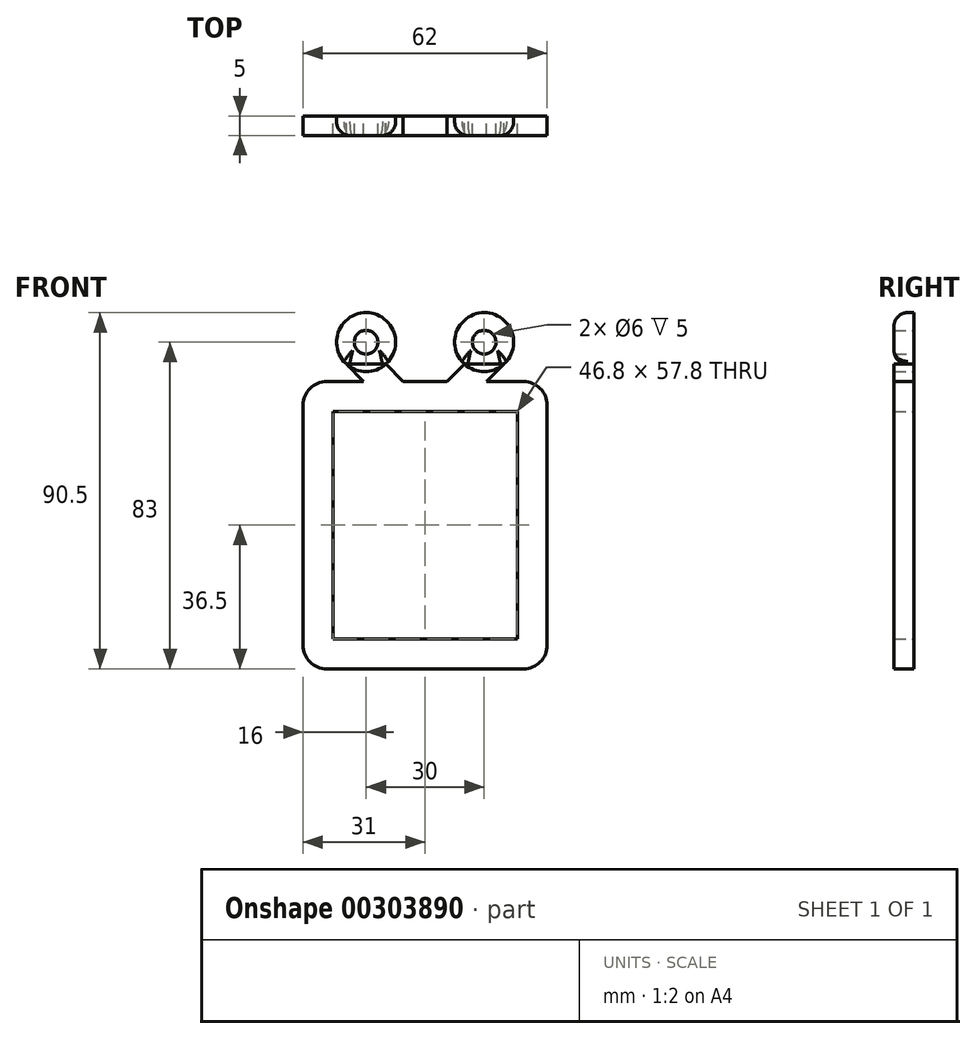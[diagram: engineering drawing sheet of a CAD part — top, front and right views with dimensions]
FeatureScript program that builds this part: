
annotation { "Feature Type Name" : "Feature", "Feature Type Description" : "" }
export const myFeature = defineFeature(function(context is Context, id is Id, definition is map)
    precondition{}
    {
        {
            var Q0;
            Q0=qCreatedBy(makeId("Front.planeOp"),FACE);
            var sketch = newSketch(context, id + "F5", { "sketchPlane" : qUnion([Q0])});
            skLineSegment(sketch, "E0.bottom", {"start": v(31, -8) * mm, "end": v(-31, -8) * mm});
            skLineSegment(sketch, "E0.top", {"start": v(31, 65) * mm, "end": v(-31, 65) * mm});
            skLineSegment(sketch, "E0.left", {"start": v(31, -8) * mm, "end": v(31, 65) * mm});
            skLineSegment(sketch, "E0.right", {"start": v(-31, -8) * mm, "end": v(-31, 65) * mm});
            skCircle(sketch, "E1", {"center": v(-15, 75) * mm, "radius": 3 * mm});
            skCircle(sketch, "E2", {"center": v(15, 75) * mm, "radius": 3 * mm});
            skLineSegment(sketch, "E3", {"start": v(0, 65) * mm, "end": v(-15, 65) * mm});
            skLineSegment(sketch, "E4", {"start": v(0, 65) * mm, "end": v(15, 65) * mm});
            skCircle(sketch, "E5", {"center": v(15, 75) * mm, "radius": 7.5 * mm});
            skCircle(sketch, "E6", {"center": v(-15, 75) * mm, "radius": 7.5 * mm});
            skLineSegment(sketch, "E7.bottom", {"start": v(-20, 69.4) * mm, "end": v(-10, 69.4) * mm});
            skLineSegment(sketch, "E7.top", {"start": v(-20, 65) * mm, "end": v(-10, 65) * mm});
            skLineSegment(sketch, "E7.left", {"start": v(-20, 69.4) * mm, "end": v(-20, 65) * mm, "construction": true});
            skLineSegment(sketch, "E7.right", {"start": v(-10, 69.4) * mm, "end": v(-10, 65) * mm, "construction": true});
            skLineSegment(sketch, "E8.bottom", {"start": v(10, 69.4) * mm, "end": v(20, 69.4) * mm});
            skLineSegment(sketch, "E8.top", {"start": v(10, 65) * mm, "end": v(20, 65) * mm});
            skLineSegment(sketch, "E8.left", {"start": v(10, 69.4) * mm, "end": v(10, 65) * mm, "construction": true});
            skLineSegment(sketch, "E8.right", {"start": v(20, 69.4) * mm, "end": v(20, 65) * mm, "construction": true});
            skLineSegment(sketch, "E9.0", {"start": v(-23, 0) * mm, "end": v(-23, 57) * mm});
            skLineSegment(sketch, "E9.1", {"start": v(23, 0) * mm, "end": v(-23, 0) * mm});
            skLineSegment(sketch, "E9.2", {"start": v(23, 0) * mm, "end": v(23, 57) * mm});
            skLineSegment(sketch, "E9.3", {"start": v(23, 57) * mm, "end": v(-23, 57) * mm});
            skLineSegment(sketch, "E10", {"start": v(-20, 69.4) * mm, "end": v(-15.6, 65) * mm});
            skLineSegment(sketch, "E11", {"start": v(20, 69.4) * mm, "end": v(15.6, 65) * mm});
            skLineSegment(sketch, "E12", {"start": v(-15, 75) * mm, "end": v(-15, 65) * mm, "construction": true});
            skLineSegment(sketch, "E13", {"start": v(15, 75) * mm, "end": v(15, 65) * mm, "construction": true});
            skLineSegment(sketch, "E14", {"start": v(-10, 69.4) * mm, "end": v(-5.6, 65) * mm});
            skLineSegment(sketch, "E15", {"start": v(10, 69.4) * mm, "end": v(5.6, 65) * mm});
            skSolve(sketch);
        }
        {
            var Q0;
            Q0=makeQuery(id+"F5.imprint","IMPRINT",FACE,{"disambiguationData":[TD([[makeQuery(id+"F5.imprint","IMPRINT",EDGE,{"derivedFrom":sQuery(id+"F5.wireOp",EDGE,"E2")}),-1.0]])]});
            var Q1;
            Q1=makeQuery(id+"F5.imprint","IMPRINT",FACE,{"disambiguationData":[TD([[makeQuery(id+"F5.imprint","IMPRINT",EDGE,{"derivedFrom":sQuery(id+"F5.wireOp",EDGE,"E1")}),-1.0]])]});
            var Q2;
            {var subQ0=sQuery(id+"F5.wireOp",EDGE,"E8.left");Q2=makeQuery(id+"F5.imprint","IMPRINT",FACE,{"disambiguationData":[TD([[makeQuery(id+"F5.imprint","IMPRINT",EDGE,{"derivedFrom":subQ0}),1.0]])]});}
            var Q3;
            Q3=makeQuery(id+"F5.imprint","IMPRINT",FACE,{"disambiguationData":[TD([[makeQuery(id+"F5.imprint","IMPRINT",EDGE,{"derivedFrom":sQuery(id+"F5.wireOp",EDGE,"E0.bottom")}),-1.0]])]});
            var Q4;
            {var subQ0=sQuery(id+"F5.wireOp",EDGE,"E7.bottom");Q4=makeQuery(id+"F5.imprint","IMPRINT",FACE,{"disambiguationData":[TD([[makeQuery(id+"F5.imprint","IMPRINT",EDGE,{"derivedFrom":subQ0}),-1.0]])]});}
            var Q5;
            {var subQ0=sQuery(id+"F5.wireOp",EDGE,"E8.bottom");Q5=makeQuery(id+"F5.imprint","IMPRINT",FACE,{"disambiguationData":[TD([[makeQuery(id+"F5.imprint","IMPRINT",EDGE,{"derivedFrom":subQ0}),-1.0]])]});}
            var Q6;
            {var subQ3=sQuery(id+"F5.wireOp",EDGE,"E7.left");Q6=makeQuery(id+"F5.imprint","IMPRINT",FACE,{"disambiguationData":[TD([[makeQuery(id+"F5.imprint","IMPRINT",EDGE,{"derivedFrom":subQ3}),1.0]])]});}
            var Q7;
            {var subQ6=sQuery(id+"F5.wireOp",EDGE,"9cc08256-3233-4f75-9d2b-67273aa2315f");Q7=makeQuery(id+"F5.imprint","IMPRINT",FACE,{"disambiguationData":[TD([[makeQuery(id+"F5.imprint","IMPRINT",EDGE,{"derivedFrom":subQ6}),-1.0]])]});}
            var Q8;
            {var subQ8=sQuery(id+"F5.wireOp",EDGE,"1ab97ab7-0e0f-4c3b-988b-f68c05d128eb");Q8=makeQuery(id+"F5.imprint","IMPRINT",FACE,{"disambiguationData":[TD([[makeQuery(id+"F5.imprint","IMPRINT",EDGE,{"derivedFrom":subQ8}),-1.0]])]});}
            extrude(context, id + "F0", {"entities" : qUnion([Q0, Q1, Q2, Q3, Q4, Q5, Q6, Q7, Q8]), "depth" : 5 * mm});
        }
        {
            var Q0;
            Q0=makeQuery(id+"F0.opExtrude","SWEPT_EDGE",EDGE,{"disambiguationData":[OSD([sQuery(id+"F5.wireOp",EDGE,"E4"),sQuery(id+"F5.wireOp",EDGE,"1ab97ab7-0e0f-4c3b-988b-f68c05d128eb")])]});
            var Q1;
            Q1=makeQuery(id+"F0.opExtrude","SWEPT_EDGE",EDGE,{"disambiguationData":[OSD([sQuery(id+"F5.wireOp",EDGE,"E5"),sQuery(id+"F5.wireOp",EDGE,"E8.bottom"),sQuery(id+"F5.wireOp",EDGE,"1ab97ab7-0e0f-4c3b-988b-f68c05d128eb")])]});
            var Q2;
            Q2=makeQuery(id+"F0.opExtrude","SWEPT_EDGE",EDGE,{"disambiguationData":[OSD([sQuery(id+"F5.wireOp",EDGE,"E5"),sQuery(id+"F5.wireOp",EDGE,"E8.bottom"),sQuery(id+"F5.wireOp",EDGE,"E11")])]});
            var Q3;
            Q3=makeQuery(id+"F0.opExtrude","SWEPT_EDGE",EDGE,{"disambiguationData":[OSD([sQuery(id+"F5.wireOp",EDGE,"E6"),sQuery(id+"F5.wireOp",EDGE,"E7.bottom"),sQuery(id+"F5.wireOp",EDGE,"E10")])]});
            var Q4;
            Q4=makeQuery(id+"F0.opExtrude","SWEPT_EDGE",EDGE,{"disambiguationData":[OSD([sQuery(id+"F5.wireOp",EDGE,"E6"),sQuery(id+"F5.wireOp",EDGE,"E7.bottom"),sQuery(id+"F5.wireOp",EDGE,"9cc08256-3233-4f75-9d2b-67273aa2315f")])]});
            var Q5;
            Q5=makeQuery(id+"F0.opExtrude","SWEPT_EDGE",EDGE,{"disambiguationData":[OSD([sQuery(id+"F5.wireOp",EDGE,"E5"),sQuery(id+"F5.wireOp",EDGE,"E8.bottom"),sQuery(id+"F5.wireOp",EDGE,"1ab97ab7-0e0f-4c3b-988b-f68c05d128eb")])]});
            var Q6;
            Q6=makeQuery(id+"F0.opExtrude","SWEPT_EDGE",EDGE,{"disambiguationData":[OSD([sQuery(id+"F5.wireOp",EDGE,"E5"),sQuery(id+"F5.wireOp",EDGE,"E8.bottom"),sQuery(id+"F5.wireOp",EDGE,"E11")])]});
            var Q7;
            Q7=makeQuery(id+"F0.opExtrude","SWEPT_EDGE",EDGE,{"disambiguationData":[OSD([sQuery(id+"F5.wireOp",EDGE,"E6"),sQuery(id+"F5.wireOp",EDGE,"E7.bottom"),sQuery(id+"F5.wireOp",EDGE,"E10")])]});
            var Q8;
            Q8=makeQuery(id+"F0.opExtrude","SWEPT_EDGE",EDGE,{"disambiguationData":[OSD([sQuery(id+"F5.wireOp",EDGE,"E6"),sQuery(id+"F5.wireOp",EDGE,"E7.bottom"),sQuery(id+"F5.wireOp",EDGE,"9cc08256-3233-4f75-9d2b-67273aa2315f")])]});
            var Q9;
            Q9=makeQuery(id+"F0.opExtrude","SWEPT_EDGE",EDGE,{"disambiguationData":[OSD([sQuery(id+"F5.wireOp",EDGE,"E7.top"),sQuery(id+"F5.wireOp",EDGE,"E10")])]});
            var Q10;
            Q10=makeQuery(id+"F0.opExtrude","SWEPT_EDGE",EDGE,{"disambiguationData":[OSD([sQuery(id+"F5.wireOp",EDGE,"E8.top"),sQuery(id+"F5.wireOp",EDGE,"E11")])]});
            var Q11;
            Q11=makeQuery(id+"F0.opExtrude","SWEPT_EDGE",EDGE,{"disambiguationData":[OSD([sQuery(id+"F5.wireOp",EDGE,"E3"),sQuery(id+"F5.wireOp",EDGE,"9cc08256-3233-4f75-9d2b-67273aa2315f")])]});
            fillet(context, id + "F1", {"entities" : qUnion([Q0, Q1, Q2, Q3, Q4, Q5, Q6, Q7, Q8, Q9, Q10, Q11]), "radius" : 2 * mm, "tangentPropagation" : true, "allowEdgeOverflow" : false});
        }
        {
            var Q0;
            Q0=makeQuery(id+"F0.opExtrude","CAP_EDGE",EDGE,{"disambiguationData":[OSD([sQuery(id+"F5.wireOp",EDGE,"E5")])],"isStart":false});
            var Q1;
            Q1=makeQuery(id+"F0.opExtrude","CAP_EDGE",EDGE,{"disambiguationData":[OSD([sQuery(id+"F5.wireOp",EDGE,"E6")])],"isStart":false});
            var Q2;
            Q2=makeQuery(id+"F0.opExtrude","CAP_EDGE",EDGE,{"disambiguationData":[OSD([sQuery(id+"F5.wireOp",EDGE,"E8.right")])],"isStart":false});
            var Q3;
            Q3=makeQuery(id+"F0.opExtrude","CAP_EDGE",EDGE,{"disambiguationData":[OSD([sQuery(id+"F5.wireOp",EDGE,"E0.left")])],"isStart":false});
            var Q4;
            Q4=makeQuery(id+"F0.opExtrude","CAP_EDGE",EDGE,{"disambiguationData":[OSD([sQuery(id+"F5.wireOp",EDGE,"E3"),sQuery(id+"F5.wireOp",EDGE,"E4")])],"isStart":false});
            var Q5;
            {var subQ0=sQuery(id+"F5.wireOp",EDGE,"E0.top");Q5=makeQuery(id+"F0.opExtrude","CAP_EDGE",EDGE,{"disambiguationData":[OSD([subQ0]),TDD([makeQuery(id+"F5.imprint","IMPRINT",EDGE,{"disambiguationData":[TD([[makeQuery(id+"F5.imprint","INTERSECT",VERTEX,{"derivedFrom":[subQ0,sQuery(id+"F5.wireOp",EDGE,"E0.right")]}),1.0]])],"derivedFrom":subQ0})])],"isStart":false});}
            var Q6;
            Q6=makeQuery(id+"F0.opExtrude","CAP_EDGE",EDGE,{"disambiguationData":[OSD([sQuery(id+"F5.wireOp",EDGE,"E7.left")])],"isStart":false});
            var Q7;
            Q7=makeQuery(id+"F0.opExtrude","CAP_EDGE",EDGE,{"disambiguationData":[OSD([sQuery(id+"F5.wireOp",EDGE,"E7.right")])],"isStart":false});
            var Q8;
            Q8=makeQuery(id+"F0.opExtrude","CAP_EDGE",EDGE,{"disambiguationData":[OSD([sQuery(id+"F5.wireOp",EDGE,"E8.left")])],"isStart":false});
            var Q9;
            Q9=makeQuery(id+"F0.opExtrude","CAP_EDGE",EDGE,{"disambiguationData":[OSD([sQuery(id+"F5.wireOp",EDGE,"E0.right")])],"isStart":false});
            var Q10;
            Q10=makeQuery(id+"F0.opExtrude","CAP_EDGE",EDGE,{"disambiguationData":[OSD([sQuery(id+"F5.wireOp",EDGE,"E0.bottom")])],"isStart":false});
            var Q11;
            {var subQ0=sQuery(id+"F5.wireOp",EDGE,"E0.top");Q11=makeQuery(id+"F0.opExtrude","CAP_EDGE",EDGE,{"disambiguationData":[OSD([subQ0]),TDD([makeQuery(id+"F5.imprint","IMPRINT",EDGE,{"disambiguationData":[TD([[makeQuery(id+"F5.imprint","INTERSECT",VERTEX,{"derivedFrom":[subQ0,sQuery(id+"F5.wireOp",EDGE,"E0.left")]}),-1.0]])],"derivedFrom":subQ0})])],"isStart":false});}
            fillet(context, id + "F2", {"entities" : qUnion([Q0, Q1, Q2, Q3, Q4, Q5, Q6, Q7, Q8, Q9, Q10, Q11]), "radius" : 3.5 * mm, "tangentPropagation" : true, "allowEdgeOverflow" : false});
        }
        {
            var Q0;
            Q0=makeQuery(id+"F0.opExtrude","SWEPT_EDGE",EDGE,{"disambiguationData":[OSD([sQuery(id+"F5.wireOp",EDGE,"E0.bottom"),sQuery(id+"F5.wireOp",EDGE,"E0.right")])]});
            var Q1;
            Q1=makeQuery(id+"F0.opExtrude","SWEPT_EDGE",EDGE,{"disambiguationData":[OSD([sQuery(id+"F5.wireOp",EDGE,"E0.top"),sQuery(id+"F5.wireOp",EDGE,"E0.right")])]});
            var Q2;
            Q2=makeQuery(id+"F0.opExtrude","SWEPT_EDGE",EDGE,{"disambiguationData":[OSD([sQuery(id+"F5.wireOp",EDGE,"E0.top"),sQuery(id+"F5.wireOp",EDGE,"E0.left")])]});
            var Q3;
            Q3=makeQuery(id+"F0.opExtrude","SWEPT_EDGE",EDGE,{"disambiguationData":[OSD([sQuery(id+"F5.wireOp",EDGE,"E0.bottom"),sQuery(id+"F5.wireOp",EDGE,"E0.left")])]});
            fillet(context, id + "F3", {"entities" : qUnion([Q0, Q1, Q2, Q3]), "radius" : 6 * mm, "tangentPropagation" : true, "allowEdgeOverflow" : false});
        }
        {
            var Q0;
            Q0=makeQuery(id+"F0.opExtrude","SWEPT_EDGE",EDGE,{"disambiguationData":[OSD([sQuery(id+"F5.wireOp",EDGE,"E9.0"),sQuery(id+"F5.wireOp",EDGE,"E9.3")])]});
            var Q1;
            Q1=makeQuery(id+"F0.opExtrude","SWEPT_EDGE",EDGE,{"disambiguationData":[OSD([sQuery(id+"F5.wireOp",EDGE,"E9.2"),sQuery(id+"F5.wireOp",EDGE,"E9.3")])]});
            var Q2;
            Q2=makeQuery(id+"F0.opExtrude","SWEPT_EDGE",EDGE,{"disambiguationData":[OSD([sQuery(id+"F5.wireOp",EDGE,"E9.1"),sQuery(id+"F5.wireOp",EDGE,"E9.2")])]});
            var Q3;
            Q3=makeQuery(id+"F0.opExtrude","SWEPT_EDGE",EDGE,{"disambiguationData":[OSD([sQuery(id+"F5.wireOp",EDGE,"E9.0"),sQuery(id+"F5.wireOp",EDGE,"E9.1")])]});
            fillet(context, id + "F6", {"entities" : qUnion([Q0, Q1, Q2, Q3]), "radius" : 1.5 * mm, "tangentPropagation" : true, "allowEdgeOverflow" : false});
        }
        {
            var Q0;
            Q0=makeQuery(id+"F5.imprint","IMPRINT",FACE,{"disambiguationData":[TD([[makeQuery(id+"F5.imprint","IMPRINT",EDGE,{"derivedFrom":sQuery(id+"F5.wireOp",EDGE,"E0.bottom")}),-1.0]])]});
            var sketch = newSketch(context, id + "F7", { "sketchPlane" : qUnion([Q0])});
            skLineSegment(sketch, "E16.0", {"start": v(23.4, -0.4) * mm, "end": v(23.4, 57.4) * mm});
            skLineSegment(sketch, "E16.1", {"start": v(23.4, -0.4) * mm, "end": v(-23.4, -0.4) * mm});
            skLineSegment(sketch, "E16.2", {"start": v(-23.4, -0.4) * mm, "end": v(-23.4, 57.4) * mm});
            skLineSegment(sketch, "E16.3", {"start": v(23.4, 57.4) * mm, "end": v(-23.4, 57.4) * mm});
            skSolve(sketch);
        }
        {
            var Q0;
            Q0=makeQuery(id+"F7.imprint","IMPRINT",FACE,{"disambiguationData":[TD([[makeQuery(id+"F7.imprint","IMPRINT",EDGE,{"derivedFrom":sQuery(id+"F7.wireOp",EDGE,"E16.0")}),1.0]])]});
            var Q1;
            Q1=makeQuery(id+"F7.imprint","IMPRINT",FACE,{"disambiguationData":[TD([[makeQuery(id+"F7.imprint","IMPRINT",EDGE,{"derivedFrom":makeQuery(id+"F5.imprint","IMPRINT",EDGE,{"derivedFrom":sQuery(id+"F5.wireOp",EDGE,"E9.0")})}),-1.0]])]});
            var Q2;
            Q2=makeQuery(id+"F0.opExtrude","CAP_FACE",FACE,{"disambiguationData":[OSD([sQuery(id+"F5.wireOp",EDGE,"E0.bottom"),sQuery(id+"F5.wireOp",EDGE,"E0.top"),sQuery(id+"F5.wireOp",EDGE,"E0.left"),sQuery(id+"F5.wireOp",EDGE,"E0.right"),sQuery(id+"F5.wireOp",EDGE,"E3"),sQuery(id+"F5.wireOp",EDGE,"E4"),sQuery(id+"F5.wireOp",EDGE,"E7.top"),sQuery(id+"F5.wireOp",EDGE,"E8.top"),sQuery(id+"F5.wireOp",EDGE,"E9.0"),sQuery(id+"F5.wireOp",EDGE,"E9.1"),sQuery(id+"F5.wireOp",EDGE,"E9.2"),sQuery(id+"F5.wireOp",EDGE,"E9.3")])],"isStart":false});
            extrude(context, id + "F4", {"entities" : qUnion([Q0, Q1]), "operationType" : NewBodyOperationType.REMOVE, "endBound" : BoundingType.UP_TO_SURFACE, "endBoundEntityFace" : qUnion([Q2]), "depth" : 25 * mm});
        }
    });
